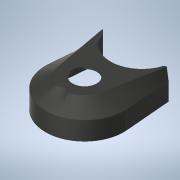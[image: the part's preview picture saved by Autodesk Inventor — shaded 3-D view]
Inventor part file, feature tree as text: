
AUTODESK INVENTOR PART (.ipt)
format: ipt  version: 2020.1 (Build 241239000, 239)  size: 1,332,224 bytes
history: native  units: mm
features: other x17, sketch x6, loft x6, extrude x5, plane x2, chamfer x2, emboss x1
ambient origin geometry x8: Origin, YZ Plane, XZ Plane, XY Plane, X Axis, Y Axis, Z Axis, Center Point
bodies: Body1 (feature_tree), Body2 (feature_tree)
feature tree (39):
  other  "Motor Holder v3 - 225 - ABS.ipt"
  plane  "Work Plane2"
  sketch  "Sketch2"  dims[d0=10.0mm d3=3.5mm]
  plane  "Work Plane1"
  extrude  "Extrusion4"  Depth=3.5mm
  sketch  "3D Sketch1"
  loft  "Loft6"
  extrude  "Extrusion5"  Depth=2.75mm
  extrude  "Extrusion6"  Depth=64.0mm
  loft  "Loft7"
  loft  "Loft8"
  loft  "Loft9"
  loft  "Loft10"
  loft  "Loft11"
  chamfer  "Chamfer3"  Distance=2.0mm
  extrude  "Extrusion7"  Depth=5.0mm TaperAngle=0.0deg
  chamfer  "Chamfer4"  Distance=1.5mm
  extrude  "Extrusion24"  Depth=16.0mm TaperAngle=0.0deg
  emboss  "Emboss1"
  other  "Solid3::Motor Holder v3 - 225 - ABS.ipt"
  other  "TaggingFeature1"
  other  "Holder Cover"
  other  "Edges1"
  other  "Edges2"
  other  "Edges3"
  other  "Edges4"
  other  "Edges5"
  other  "Edges6"
  other  "Edges7"
  other  "Edges8"
  other  "Edges9"
  sketch  "3D Sketch2"
  sketch  "Sketch8"  dims[d4=3.5mm d5=21.0mm]
  sketch  "Sketch24"  dims[d6=2.5mm d14=2.75mm d15=2.75mm]
  sketch  "Sketch28"  dims[d24=-7.25mm d26=64.0mm d28=32.0mm d29=1.5mm d41=0.5mm d43=0.5mm d51=2.0mm d52=2.0mm d67=5.0mm d68=0.0mm d73=1.5mm d74=0.0mm d75=16.0mm d76=0.0mm d81=29.698599mm d88=0.858664mm d91=1.296614mm d92=45.0deg d97=3.5mm d100=3.5mm d103=0.0mm d104=90.0deg d105=0.0mm d106=90.0deg d107=0.0mm d108=90.0deg d109=0.0mm d110=90.0deg d111=0.0mm d112=90.0deg d113=0.0mm d114=90.0deg d115=0.0mm d116=90.0deg d117=0.0mm d118=90.0deg d119=0.0mm d120=90.0deg d121=0.0mm d122=90.0deg d123=0.0mm d124=90.0deg d125=0.0mm d126=90.0deg d127=0.5mm d128=1.5mm d129=45.0deg d130=23.0mm d131=0.0mm d132=0.5mm d133=1.5mm d134=45.0deg d146=2.75mm d170=52.0mm d171=2.0mm d264=2.0mm d267=2.0mm d294=1.452114mm d295=1.452114mm d304=1.452114mm d305=1.452114mm d329=15.0mm d330=0.0mm d331=5.0mm d332=5.0mm d333=5.0mm d335=0.4mm d336=0.0mm d337=0.0mm d338=90.0deg d339=0.0mm d340=90.0deg]
  other  "Edges10"
  other  "Edges11"
  other  "Edges12"
  other  "Holder"
